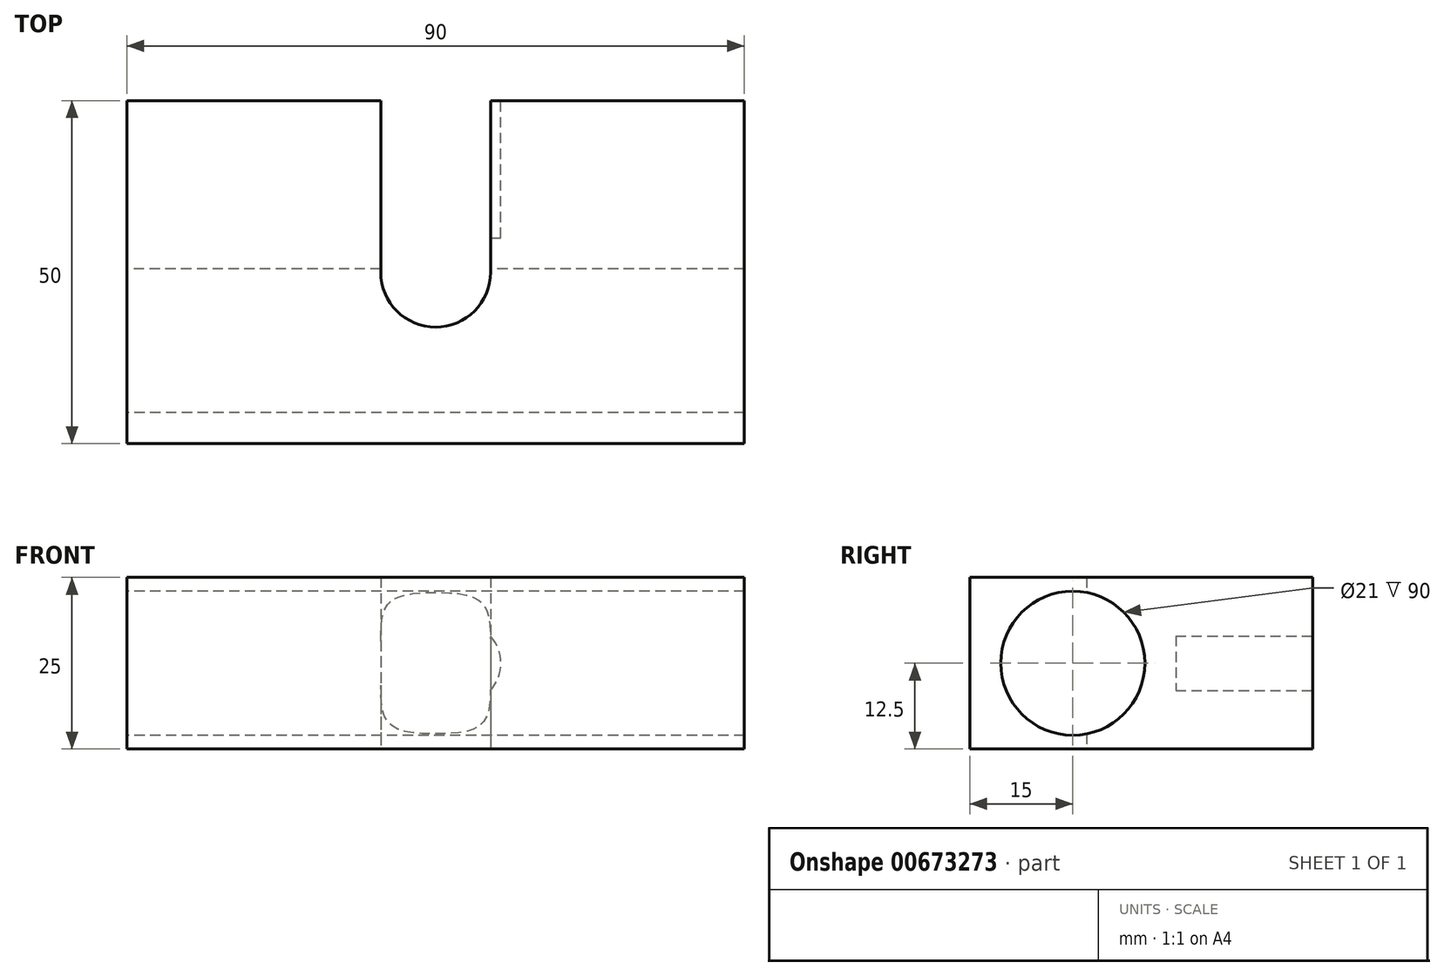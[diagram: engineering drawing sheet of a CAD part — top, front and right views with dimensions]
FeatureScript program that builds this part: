
annotation { "Feature Type Name" : "Feature", "Feature Type Description" : "" }
export const myFeature = defineFeature(function(context is Context, id is Id, definition is map)
    precondition{}
    {
        {
            var Q0;
            Q0=qCreatedBy(makeId("Top.planeOp"),FACE);
            var sketch = newSketch(context, id + "F0", { "sketchPlane" : qUnion([Q0])});
            skLineSegment(sketch, "E0.bottom", {"start": v(0, 0) * mm, "end": v(90, 0) * mm});
            skLineSegment(sketch, "E0.top", {"start": v(0, 50) * mm, "end": v(90, 50) * mm});
            skLineSegment(sketch, "E0.left", {"start": v(0, 0) * mm, "end": v(0, 50) * mm});
            skLineSegment(sketch, "E0.right", {"start": v(90, 0) * mm, "end": v(90, 50) * mm});
            skLineSegment(sketch, "E1", {"start": v(45, 50) * mm, "end": v(45, 0) * mm, "construction": true});
            skLineSegment(sketch, "E2", {"start": v(0, 25) * mm, "end": v(90, 25) * mm, "construction": true});
            skLineSegment(sketch, "E3", {"start": v(37, 25) * mm, "end": v(37, 50) * mm});
            skLineSegment(sketch, "E4", {"start": v(53, 25) * mm, "end": v(53, 50) * mm});
            skArc(sketch, "E5", {"start": v(37, 25) * mm, "mid": v(45, 17) * mm, "end": v(53, 25) * mm});
            skSolve(sketch);
        }
        {
            var Q0;
            Q0=makeQuery(id+"F0.imprint","IMPRINT",FACE,{"disambiguationData":[TD([[makeQuery(id+"F0.imprint","IMPRINT",EDGE,{"derivedFrom":sQuery(id+"F0.wireOp",EDGE,"E0.bottom")}),1.0]])]});
            extrude(context, id + "F1", {"entities" : qUnion([Q0]), "depth" : 25 * mm, "offsetDistance" : 25 * mm});
        }
        {
            var Q0;
            Q0=makeQuery(id+"F1.opExtrude","SWEPT_FACE",FACE,{"disambiguationData":[OSD([sQuery(id+"F0.wireOp",EDGE,"E0.left")])]});
            var sketch = newSketch(context, id + "F2", { "sketchPlane" : qUnion([Q0])});
            skCircle(sketch, "E6", {"center": v(-15, 12.5) * mm, "radius": 10.5 * mm});
            skLineSegment(sketch, "E7", {"start": v(0, 12.5) * mm, "end": v(-50, 12.5) * mm, "construction": true});
            skSolve(sketch);
        }
        {
            var Q0;
            Q0=makeQuery(id+"F2.imprint","IMPRINT",FACE,{"disambiguationData":[TD([[makeQuery(id+"F2.imprint","IMPRINT",EDGE,{"derivedFrom":sQuery(id+"F2.wireOp",EDGE,"E6")}),1.0]])]});
            extrude(context, id + "F3", {"entities" : qUnion([Q0]), "operationType" : NewBodyOperationType.REMOVE, "endBound" : BoundingType.THROUGH_ALL, "oppositeDirection" : true, "depth" : 25 * mm, "offsetDistance" : 25 * mm});
        }
        {
            var Q0;
            Q0=makeQuery(id+"F1.opExtrude","SWEPT_FACE",FACE,{"disambiguationData":[OSD([sQuery(id+"F0.wireOp",EDGE,"E0.top")])]});
            var sketch = newSketch(context, id + "F4", { "sketchPlane" : qUnion([Q0])});
            skCircle(sketch, "E8", {"center": v(-48.5, 12.5) * mm, "radius": 6 * mm});
            skCircle(sketch, "E9", {"center": v(11.5, 12.5) * mm, "radius": 6 * mm});
            skLineSegment(sketch, "E10", {"start": v(-90, 12.5) * mm, "end": v(0, 12.5) * mm, "construction": true});
            skLineSegment(sketch, "E11", {"start": v(-18.5, 25) * mm, "end": v(-18.5, 0) * mm, "construction": true});
            skSolve(sketch);
        }
        {
            var Q0;
            Q0=makeQuery(id+"F4.imprint","IMPRINT",FACE,{"disambiguationData":[TD([[makeQuery(id+"F4.imprint","IMPRINT",EDGE,{"derivedFrom":sQuery(id+"F4.wireOp",EDGE,"E8")}),1.0]])]});
            var Q1;
            Q1=makeQuery(id+"F4.imprint","IMPRINT",FACE,{"disambiguationData":[TD([[makeQuery(id+"F4.imprint","IMPRINT",EDGE,{"derivedFrom":sQuery(id+"F4.wireOp",EDGE,"E9")}),1.0]])]});
            extrude(context, id + "F5", {"entities" : qUnion([Q0, Q1]), "operationType" : NewBodyOperationType.REMOVE, "oppositeDirection" : true, "depth" : 20 * mm, "offsetDistance" : 25 * mm});
        }
    });
